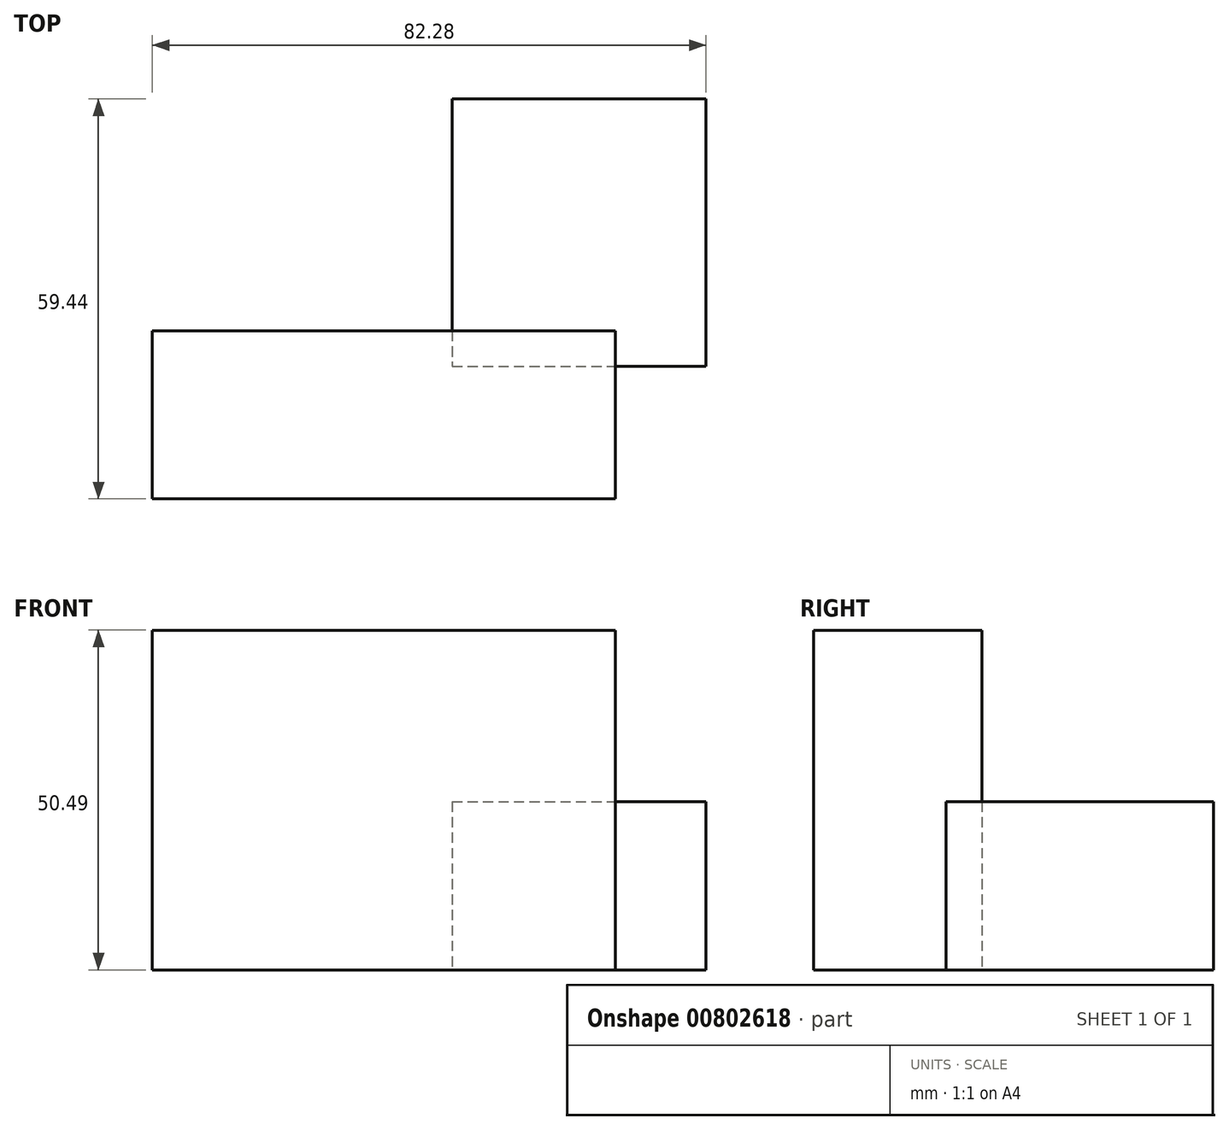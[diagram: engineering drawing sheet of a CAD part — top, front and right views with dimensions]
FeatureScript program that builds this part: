
annotation { "Feature Type Name" : "Feature", "Feature Type Description" : "" }
export const myFeature = defineFeature(function(context is Context, id is Id, definition is map)
    precondition{}
    {
        {
            var Q0;
            Q0=qCreatedBy(makeId("Top.planeOp"),FACE);
            var sketch = newSketch(context, id + "F0", { "sketchPlane" : qUnion([Q0])});
            skLineSegment(sketch, "E0.bottom", {"start": v(-65.56, 34.44) * mm, "end": v(-27.83, 34.44) * mm});
            skLineSegment(sketch, "E0.top", {"start": v(-65.56, -5.29) * mm, "end": v(-27.83, -5.29) * mm});
            skLineSegment(sketch, "E0.left", {"start": v(-65.56, 34.44) * mm, "end": v(-65.56, -5.29) * mm});
            skLineSegment(sketch, "E0.right", {"start": v(-27.83, 34.44) * mm, "end": v(-27.83, -5.29) * mm});
            skSolve(sketch);
        }
        {
            var Q0;
            Q0=qCreatedBy(makeId("Front.planeOp"),FACE);
            var sketch = newSketch(context, id + "F1", { "sketchPlane" : qUnion([Q0])});
            skLineSegment(sketch, "E1.bottom", {"start": v(-110.11, 50.49) * mm, "end": v(-41.31, 50.49) * mm});
            skLineSegment(sketch, "E1.top", {"start": v(-110.11, 0) * mm, "end": v(-41.31, 0) * mm});
            skLineSegment(sketch, "E1.left", {"start": v(-110.11, 50.49) * mm, "end": v(-110.11, 0) * mm});
            skLineSegment(sketch, "E1.right", {"start": v(-41.31, 50.49) * mm, "end": v(-41.31, 0) * mm});
            skSolve(sketch);
        }
        {
            var Q0;
            Q0 = qSketchRegion(id + "F1", true);
            extrude(context, id + "F2", {"entities" : qUnion([Q0]), "depth" : 25 * mm, "offsetDistance" : 25 * mm});
        }
        {
            var Q0;
            Q0 = qSketchRegion(id + "F0", true);
            extrude(context, id + "F3", {"entities" : qUnion([Q0]), "depth" : 25 * mm, "offsetDistance" : 25 * mm});
        }
    });
